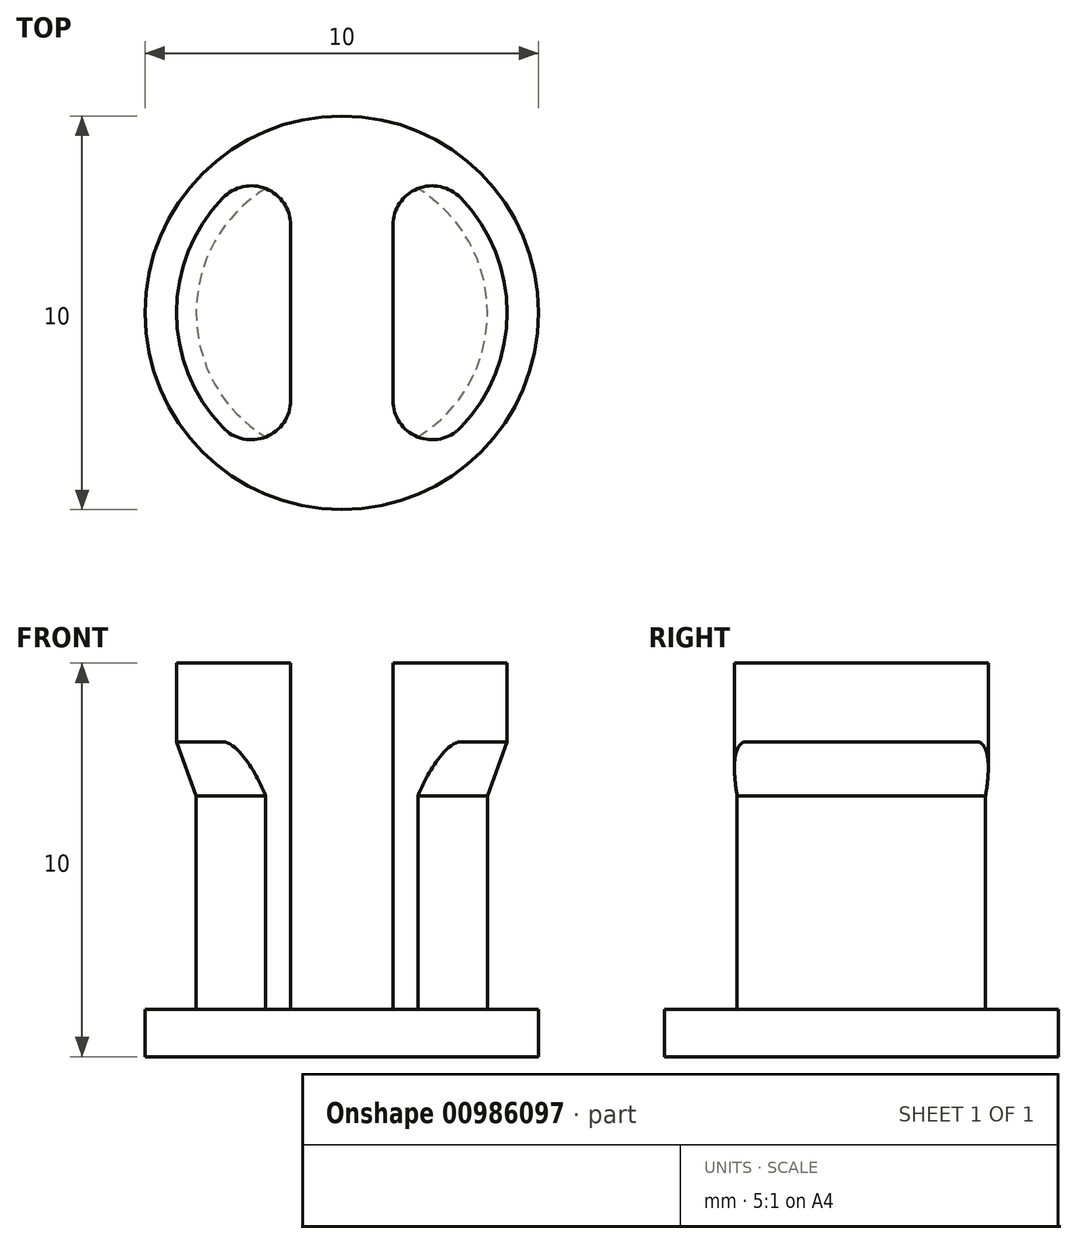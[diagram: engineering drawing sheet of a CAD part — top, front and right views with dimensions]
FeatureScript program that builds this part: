
annotation { "Feature Type Name" : "Feature", "Feature Type Description" : "" }
export const myFeature = defineFeature(function(context is Context, id is Id, definition is map)
    precondition{}
    {
        {
            var Q0;
            Q0=qCreatedBy(makeId("Front.planeOp"),FACE);
            var sketch = newSketch(context, id + "F0", { "sketchPlane" : qUnion([Q0])});
            skLineSegment(sketch, "E0", {"start": v(0, 0) * mm, "end": v(-5, 0) * mm});
            skLineSegment(sketch, "E1", {"start": v(-5, 0) * mm, "end": v(-5, 1.2) * mm});
            skLineSegment(sketch, "E2", {"start": v(-5, 1.2) * mm, "end": v(-3.7, 1.2) * mm});
            skLineSegment(sketch, "E3", {"start": v(-3.7, 1.2) * mm, "end": v(-3.7, 10) * mm});
            skLineSegment(sketch, "E4", {"start": v(-3.7, 10) * mm, "end": v(0, 10) * mm});
            skLineSegment(sketch, "E5", {"start": v(0, 0) * mm, "end": v(0, 10) * mm});
            skLineSegment(sketch, "E6", {"start": v(-3.7, 6.63) * mm, "end": v(-4.2, 8) * mm});
            skLineSegment(sketch, "E7", {"start": v(-4.2, 8) * mm, "end": v(-4.2, 10) * mm});
            skLineSegment(sketch, "E8", {"start": v(-4.2, 10) * mm, "end": v(-3.7, 10) * mm});
            skLineSegment(sketch, "E9", {"start": v(0, 10) * mm, "end": v(0, 17.06) * mm, "construction": true});
            skSolve(sketch);
        }
        {
            var Q0;
            Q0=makeQuery(id+"F0.imprint","IMPRINT",FACE,{"disambiguationData":[TD([[makeQuery(id+"F0.imprint","IMPRINT",EDGE,{"derivedFrom":sQuery(id+"F0.wireOp",EDGE,"E0")}),-1.0]])]});
            var Q1;
            {var subQ2=sQuery(id+"F0.wireOp",EDGE,"E6");Q1=makeQuery(id+"F0.imprint","IMPRINT",FACE,{"disambiguationData":[TD([[makeQuery(id+"F0.imprint","IMPRINT",EDGE,{"derivedFrom":subQ2}),-1.0]])]});}
            var Q2;
            Q2=sQuery(id+"F0.wireOp",EDGE,"E5");
            revolve(context, id + "F1", {"surfaceOperationType" : NewSurfaceOperationType.NEW, "entities" : qUnion([Q0, Q1]), "axis" : qUnion([Q2]), "revolveType" : RevolveType.FULL});
        }
        {
            var Q0;
            Q0=makeQuery(id+"F1.opRevolve","SWEPT_FACE",FACE,{"disambiguationData":[OSD([sQuery(id+"F0.wireOp",EDGE,"E4")])]});
            var sketch = newSketch(context, id + "F2", { "sketchPlane" : qUnion([Q0])});
            skLineSegment(sketch, "E10", {"start": v(-1.3, 4.83) * mm, "end": v(-1.3, -4.83) * mm});
            skLineSegment(sketch, "E11", {"start": v(1.3, -4.83) * mm, "end": v(1.3, 4.83) * mm});
            skLineSegment(sketch, "E12", {"start": v(-1.3, 0) * mm, "end": v(1.3, 0) * mm, "construction": true});
            skCircle(sketch, "E13.0", {"center": v(0, 0) * mm, "radius": 5 * mm});
            skSolve(sketch);
        }
        {
            var Q0;
            {var subQ0=sQuery(id+"F2.wireOp",EDGE,"E10");Q0=makeQuery(id+"F2.imprint","IMPRINT",FACE,{"disambiguationData":[TD([[makeQuery(id+"F2.imprint","IMPRINT",EDGE,{"derivedFrom":subQ0}),1.0]])]});}
            var Q1;
            Q1=makeQuery(id+"F1.opRevolve","SWEPT_FACE",FACE,{"disambiguationData":[OSD([sQuery(id+"F0.wireOp",EDGE,"E2")])]});
            extrude(context, id + "F3", {"entities" : qUnion([Q0]), "operationType" : NewBodyOperationType.REMOVE, "endBound" : BoundingType.UP_TO_SURFACE, "oppositeDirection" : true, "depth" : 8 * mm, "endBoundEntityFace" : qUnion([Q1]), "offsetDistance" : 25 * mm});
        }
        {
            var Q0;
            Q0=makeQuery(id+"F3.boolean.opBoolean","INTERSECT",EDGE,{"disambiguationData":[OD(0.0)],"derivedFrom":[makeQuery(id+"F1.opRevolve","SWEPT_FACE",FACE,{"disambiguationData":[OSD([sQuery(id+"F0.wireOp",EDGE,"E7")])]}),makeQuery(id+"F3.opExtrude","SWEPT_FACE",FACE,{"disambiguationData":[OSD([sQuery(id+"F2.wireOp",EDGE,"E10")])]})]});
            var Q1;
            Q1=makeQuery(id+"F3.boolean.opBoolean","INTERSECT",EDGE,{"disambiguationData":[OD(1.0)],"derivedFrom":[makeQuery(id+"F1.opRevolve","SWEPT_FACE",FACE,{"disambiguationData":[OSD([sQuery(id+"F0.wireOp",EDGE,"E7")])]}),makeQuery(id+"F3.opExtrude","SWEPT_FACE",FACE,{"disambiguationData":[OSD([sQuery(id+"F2.wireOp",EDGE,"E10")])]})]});
            var Q2;
            Q2=makeQuery(id+"F3.boolean.opBoolean","INTERSECT",EDGE,{"disambiguationData":[OD(0.0)],"derivedFrom":[makeQuery(id+"F1.opRevolve","SWEPT_FACE",FACE,{"disambiguationData":[OSD([sQuery(id+"F0.wireOp",EDGE,"E7")])]}),makeQuery(id+"F3.opExtrude","SWEPT_FACE",FACE,{"disambiguationData":[OSD([sQuery(id+"F2.wireOp",EDGE,"E11")])]})]});
            var Q3;
            Q3=makeQuery(id+"F3.boolean.opBoolean","INTERSECT",EDGE,{"disambiguationData":[OD(1.0)],"derivedFrom":[makeQuery(id+"F1.opRevolve","SWEPT_FACE",FACE,{"disambiguationData":[OSD([sQuery(id+"F0.wireOp",EDGE,"E7")])]}),makeQuery(id+"F3.opExtrude","SWEPT_FACE",FACE,{"disambiguationData":[OSD([sQuery(id+"F2.wireOp",EDGE,"E11")])]})]});
            fillet(context, id + "F4", {"entities" : qUnion([Q0, Q1, Q2, Q3]), "radius" : 1 * mm, "tangentPropagation" : true, "allowEdgeOverflow" : false});
        }
    });
